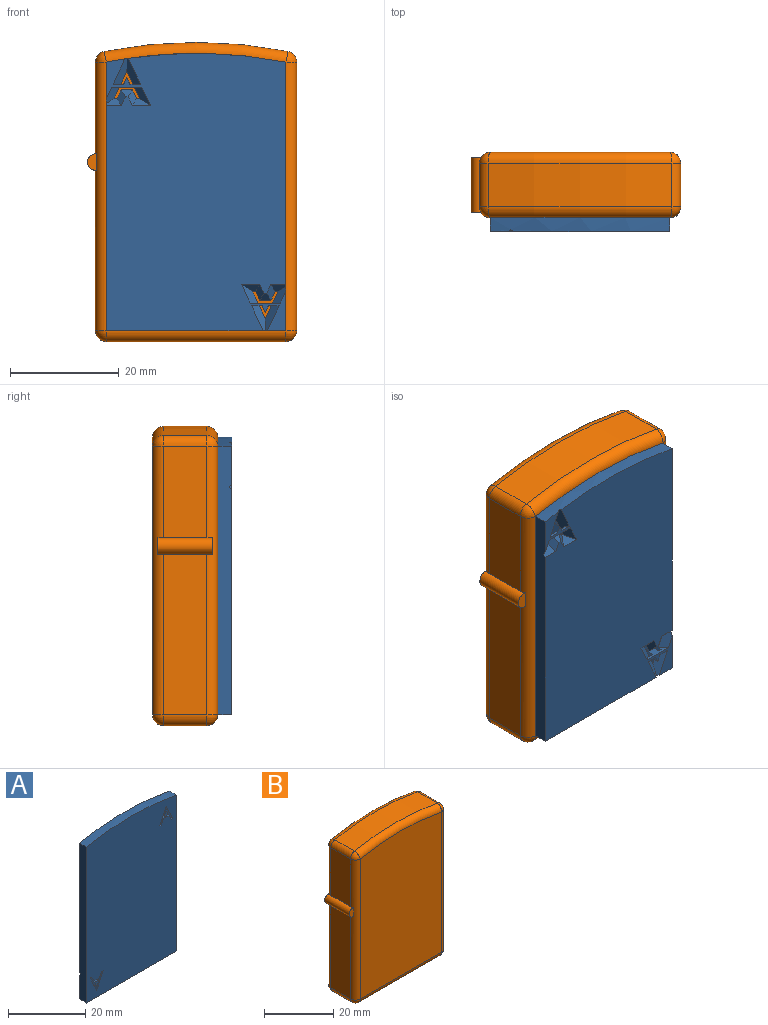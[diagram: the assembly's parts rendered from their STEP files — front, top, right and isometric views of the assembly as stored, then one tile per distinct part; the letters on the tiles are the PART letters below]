
ASSEMBLY  parts=2 mates=1
PART A: 51 faces, bbox 33x2.5x51 mm
  f0: plane 51x33mm, normal (0,-1,0), area 1650.5mm2, adj f2,f12,f13,f14,f15,f16,f17,f18
  f1: plane 51x33mm, normal (0,1,0), area 1595.7mm2, adj f2,f3,f5,f6,f7,f8,f9,f10
  f2: plane 33x2.54mm, normal (0,0,-1), area 83.7mm2, adj f0,f1,f13,f41,f42,f50
  f3: plane 2.77x1.27mm, normal (0,0.71,0.71), area 3.4mm2, adj f1,f14,f47,f48,f50
  f4: plane 1.72x1.6mm, normal (0,-1,0), area 1.4mm2, adj f8,f28,f31
  f5: plane 5.53x2.54mm, normal (0,0,-1), area 5.8mm2, adj f1,f11,f19,f20,f34,f35,f47,f49
  f6: plane 1.96x0.51mm, normal (0,0,1), area 0.9mm2, adj f1,f19,f35,f47
  f7: plane 1.96x0.51mm, normal (0,0,1), area 0.9mm2, adj f1,f20,f34,f49
  f8: plane 5.53x2.54mm, normal (0,0,1), area 6.1mm2, adj f1,f4,f28,f30,f31,f32,f33,f41
  f9: plane 1.96x0.51mm, normal (0,0,-1), area 0.9mm2, adj f1,f28,f33,f41
  f10: plane 1.96x1.27mm, normal (0,0,-1), area 1.2mm2, adj f1,f30,f31,f32,f42
  f11: plane 1.72x1.6mm, normal (0,-1,0), area 1.4mm2, adj f5,f19,f20
  f12: cylinder r=84.56mm len=33mm, axis (0,1,0), area 84.3mm2, adj f0,f1,f13,f47,f49,f50
  f13: plane 49.37x2.54mm, normal (-1,0,0), area 125.2mm2, adj f0,f1,f2,f12,f36,f43
  f14: plane 1.27x0.56mm, normal (0,0,1), area 0.7mm2, adj f0,f3,f15,f22
  f15: plane 1.65x1.27mm, normal (0.91,0,0.42), area 2.3mm2, adj f0,f14,f16,f48
  f16: plane 2.08x1.27mm, normal (0,0,1), area 2.6mm2, adj f0,f15,f17,f46
  f17: plane 1.65x1.27mm, normal (-0.91,0,0.42), area 2.3mm2, adj f0,f16,f18,f45
  f18: plane 1.27x0.56mm, normal (0,0,1), area 0.7mm2, adj f0,f17,f21,f44
  f19: plane 2.54x1.72mm, normal (0.91,0,0.42), area 4.5mm2, adj f1,f5,f6,f11,f20,f35
  f20: plane 2.54x1.72mm, normal (-0.91,0,0.42), area 4.5mm2, adj f1,f5,f7,f11,f19,f34
  f21: plane 5.08x2.37mm, normal (0.91,0,-0.42), area 7.1mm2, adj f0,f18,f22,f49
  f22: plane 5.08x2.37mm, normal (-0.91,0,-0.42), area 7.1mm2, adj f0,f14,f21,f47
  f23: plane 1.27x0.56mm, normal (0,0,-1), area 0.7mm2, adj f0,f24,f30,f36
  f24: plane 1.65x1.27mm, normal (-0.91,0,-0.42), area 2.3mm2, adj f0,f23,f25,f37
  f25: plane 2.08x1.27mm, normal (0,0,-1), area 2.6mm2, adj f0,f24,f26,f38
  f26: plane 1.65x1.27mm, normal (0.91,0,-0.42), area 2.3mm2, adj f0,f25,f27,f39
  f27: plane 1.27x0.56mm, normal (0,0,-1), area 0.7mm2, adj f0,f26,f29,f40
  f28: plane 2.54x1.72mm, normal (0.91,0,-0.42), area 4.5mm2, adj f1,f4,f8,f9,f31,f33
  f29: plane 5.08x2.37mm, normal (-0.91,0,0.42), area 7.1mm2, adj f0,f27,f30,f41
  f30: plane 5.08x2.37mm, normal (0.91,0,0.42), area 7.5mm2, adj f0,f8,f10,f23,f29,f32,f42,f43
  f31: plane 2.54x1.72mm, normal (-0.91,0,-0.42), area 4.5mm2, adj f1,f4,f8,f10,f28,f32
  f32: plane 0.8x0.51mm, normal (0,-1,0), area 0.3mm2, adj f8,f10,f30,f31
  f33: plane 1.64x0.51mm, normal (0,-1,0), area 0.7mm2, adj f8,f9,f28,f41
  f34: plane 1.64x0.51mm, normal (0,-1,0), area 0.7mm2, adj f5,f7,f20,f49
  f35: plane 1.64x0.51mm, normal (0,-1,0), area 0.7mm2, adj f5,f6,f19,f47
  f36: plane 2.77x1.27mm, normal (0,0.71,-0.71), area 3.4mm2, adj f1,f13,f23,f37,f43
  f37: plane 2.92x1.58mm, normal (-0.64,0.71,-0.3), area 3.3mm2, adj f1,f24,f36,f38
  f38: plane 2.08x1.27mm, normal (0,0.71,-0.71), area 2.3mm2, adj f1,f25,f37,f39
  f39: plane 2.92x1.58mm, normal (0.64,0.71,-0.3), area 3.3mm2, adj f1,f26,f38,f40
  f40: plane 3.36x1.27mm, normal (0,0.71,-0.71), area 3.5mm2, adj f1,f27,f39,f41
  f41: plane 8.51x4.36mm, normal (-0.64,0.71,0.3), area 13.7mm2, adj f1,f2,f8,f9,f29,f33,f40,f42
  f42: plane 4.57x2.53mm, normal (0.64,0.71,0.3), area 7.5mm2, adj f1,f2,f10,f30,f41
  f43: plane 3.05x2.4mm, normal (0.64,0.71,0.3), area 5.2mm2, adj f1,f8,f13,f30,f36
  f44: plane 3.36x1.27mm, normal (0,0.71,0.71), area 3.5mm2, adj f1,f18,f45,f49
  f45: plane 2.92x1.58mm, normal (-0.64,0.71,0.3), area 3.3mm2, adj f1,f17,f44,f46
  f46: plane 2.08x1.27mm, normal (0,0.71,0.71), area 2.3mm2, adj f1,f16,f45,f48
  f47: plane 8.28x3.77mm, normal (-0.64,0.71,-0.3), area 13.4mm2, adj f1,f3,f5,f6,f12,f22,f35,f49
  f48: plane 2.92x1.58mm, normal (0.64,0.71,0.3), area 3.3mm2, adj f1,f3,f15,f46
  f49: plane 8.71x4.36mm, normal (0.64,0.71,-0.3), area 13.8mm2, adj f1,f5,f7,f12,f21,f34,f44,f47
  f50: plane 49.37x2.54mm, normal (1,0,0), area 125.2mm2, adj f0,f1,f2,f3,f12,f47
PART B: 30 faces, bbox 38.5x12x62.1 mm
  f0: plane 16.87x8mm, normal (-1,0,0), area 135mm2, adj f2,f3,f26,f27
  f1: plane 29.5x8mm, normal (-1,0,0), area 236mm2, adj f2,f3,f14,f27
  f2: cylinder r=2mm len=49.37mm, axis (0,0,1), area 152mm2, adj f0,f1,f7,f19,f24,f27,f28
  f3: cylinder r=2mm len=49.37mm, axis (0,0,-1), area 152mm2, adj f0,f1,f8,f20,f25,f27,f29
  f4: plane 49.37x8mm, normal (1,0,0), area 395mm2, adj f9,f12,f16,f17
  f5: cylinder r=86.56mm len=33.78mm, axis (0,1,0), area 272mm2, adj f17,f22,f23,f26
  f6: plane 33x8mm, normal (0,0,-1), area 264mm2, adj f9,f13,f14,f15
  f7: plane 51x33mm, normal (0,-1,0), area 1665.2mm2, adj f2,f12,f13,f22
  f8: plane 51x33mm, normal (0,1,0), area 1665.2mm2, adj f3,f15,f16,f23
  f9: cylinder r=2mm len=8mm, axis (0,1,0), area 25.1mm2, adj f4,f6,f10,f11
  f10: sphere r=2mm, area 6.3mm2, adj f9,f12,f13
  f11: sphere r=2mm, area 6.3mm2, adj f9,f15,f16
  f12: cylinder r=2mm len=49.37mm, axis (0,0,-1), area 155.1mm2, adj f4,f7,f10,f18
  f13: cylinder r=2mm len=33mm, axis (-1,0,0), area 103.7mm2, adj f6,f7,f10,f19
  f14: cylinder r=2mm len=8mm, axis (0,-1,0), area 25.1mm2, adj f1,f6,f19,f20
  f15: cylinder r=2mm len=33mm, axis (1,0,0), area 103.7mm2, adj f6,f8,f11,f20
  f16: cylinder r=2mm len=49.37mm, axis (0,0,1), area 155.1mm2, adj f4,f8,f11,f21
  f17: cylinder r=2mm len=8mm, axis (0,1,0), area 22mm2, adj f4,f5,f18,f21
  f18: sphere r=2mm, area 5.5mm2, adj f12,f17,f22
  f19: sphere r=2mm, area 6.3mm2, adj f2,f13,f14
  f20: sphere r=2mm, area 6.3mm2, adj f3,f14,f15
  f21: sphere r=2mm, area 5.5mm2, adj f16,f17,f23
  f22: torus R=84.56mm, axis (0,-1,0), area 105.9mm2, adj f5,f7,f18,f24
  f23: torus R=84.56mm, axis (0,-1,0), area 105.9mm2, adj f5,f8,f21,f25
  f24: sphere r=2mm, area 5.5mm2, adj f2,f22,f26
  f25: sphere r=2mm, area 5.5mm2, adj f3,f23,f26
  f26: cylinder r=2mm len=8mm, axis (0,1,0), area 22mm2, adj f0,f5,f24,f25
  f27: cylinder r=1.5mm len=10mm, axis (0,1,0), area 47.5mm2, adj f0,f1,f2,f3,f28,f29
  f28: plane 3x1.77mm, normal (0,-1,0), area 4.3mm2, adj f2,f27
  f29: plane 3x1.77mm, normal (0,1,0), area 4.3mm2, adj f3,f27
PLACE A rot(axis=(0,0,1),180deg) t=(-25.79,-7.51,-15.69)mm
PLACE B t=(-27.79,7.03,-17.69)mm
MATE fastened A.f0 <-> B.f7  axis (0,1,0) through (-9.29,-4.97,9.54)mm
